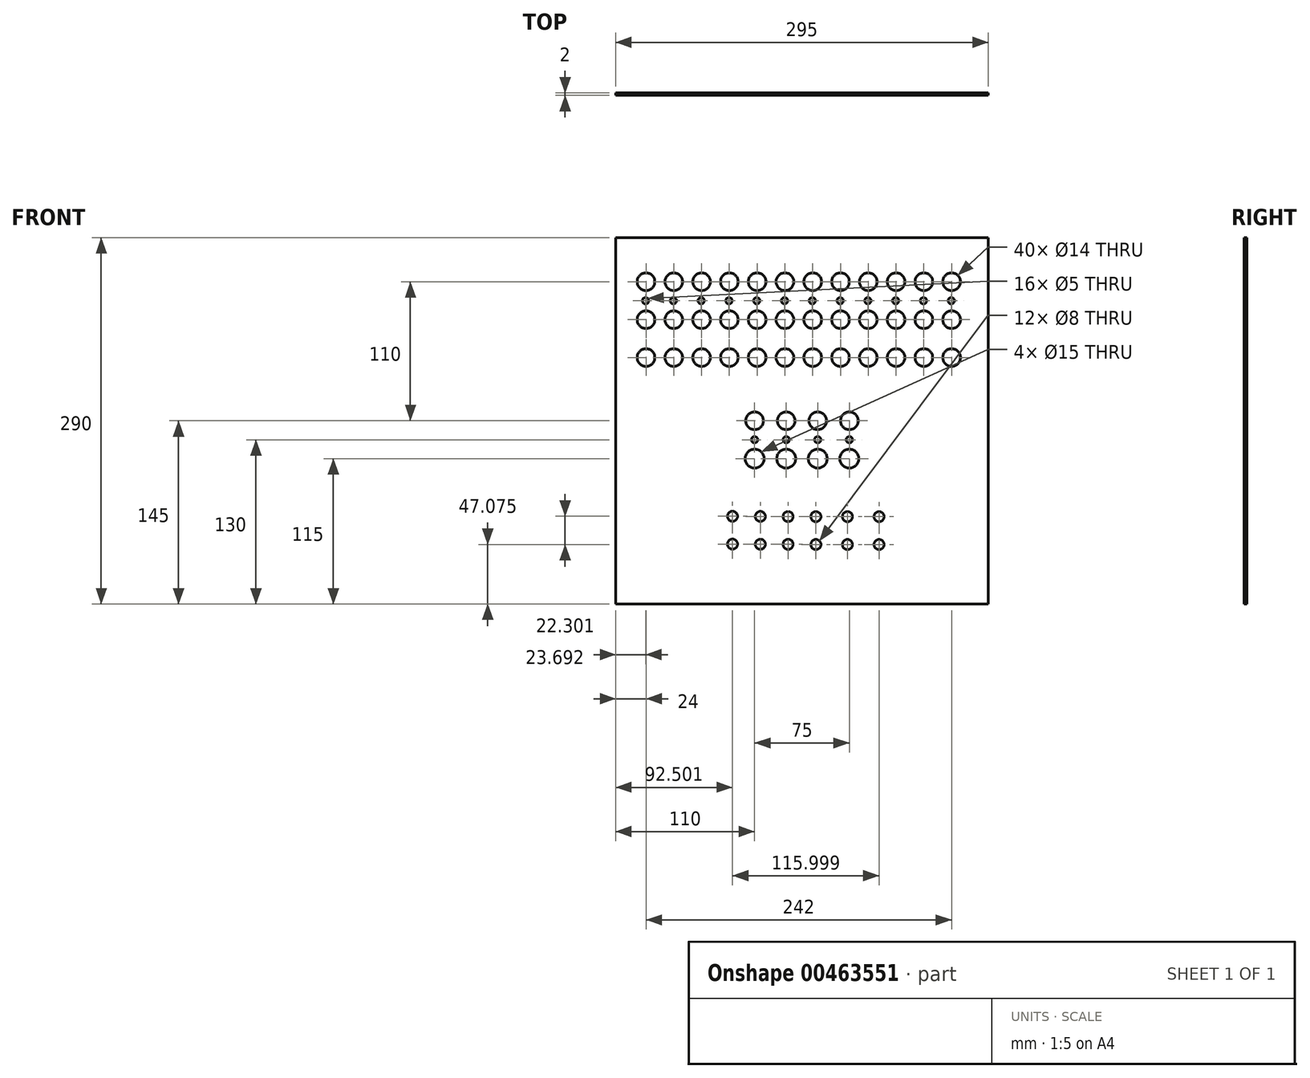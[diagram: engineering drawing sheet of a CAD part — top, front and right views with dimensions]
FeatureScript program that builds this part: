
annotation { "Feature Type Name" : "Feature", "Feature Type Description" : "" }
export const myFeature = defineFeature(function(context is Context, id is Id, definition is map)
    precondition{}
    {
        {
            var Q0;
            Q0=qCreatedBy(makeId("Front.planeOp"),FACE);
            var sketch = newSketch(context, id + "F0", { "sketchPlane" : qUnion([Q0])});
            skLineSegment(sketch, "E0.bottom", {"start": v(147.5, 145) * mm, "end": v(-147.5, 145) * mm});
            skLineSegment(sketch, "E0.top", {"start": v(147.5, -145) * mm, "end": v(-147.5, -145) * mm});
            skLineSegment(sketch, "E0.left", {"start": v(147.5, 145) * mm, "end": v(147.5, -145) * mm});
            skLineSegment(sketch, "E0.right", {"start": v(-147.5, 145) * mm, "end": v(-147.5, -145) * mm});
            skPoint(sketch, "E0.middle", {"position": v(0, 0) * mm});
            skSolve(sketch);
        }
        {
            var Q0;
            Q0=makeQuery(id+"F0.imprint","IMPRINT",FACE,{"disambiguationData":[TD([[makeQuery(id+"F0.imprint","IMPRINT",EDGE,{"derivedFrom":sQuery(id+"F0.wireOp",EDGE,"E0.bottom")}),1.0]])]});
            extrude(context, id + "F1", {"entities" : qUnion([Q0]), "oppositeDirection" : true, "depth" : 2 * mm, "offsetDistance" : 25 * mm});
        }
        {
            var Q0;
            Q0=makeQuery(id+"F1.opExtrude","CAP_FACE",FACE,{"disambiguationData":[OSD([sQuery(id+"F0.wireOp",EDGE,"E0.bottom"),sQuery(id+"F0.wireOp",EDGE,"E0.top"),sQuery(id+"F0.wireOp",EDGE,"E0.left"),sQuery(id+"F0.wireOp",EDGE,"E0.right")])],"isStart":true});
            var sketch = newSketch(context, id + "F2", { "sketchPlane" : qUnion([Q0])});
            skLineSegment(sketch, "E1", {"start": v(-147.5, 110) * mm, "end": v(322.56, 110) * mm});
            skCircle(sketch, "E2", {"center": v(-123.5, 110) * mm, "radius": 7 * mm});
            skLineSegment(sketch, "E3.direction1", {"start": v(-120.5, 110) * mm, "end": v(-98.5, 110) * mm, "construction": true});
            skCircle(sketch, "E4.1.0.0", {"center": v(-101.5, 110) * mm, "radius": 7 * mm});
            skCircle(sketch, "E4.2.0.0", {"center": v(-79.5, 110) * mm, "radius": 7 * mm});
            skCircle(sketch, "E4.3.0.0", {"center": v(-57.5, 110) * mm, "radius": 7 * mm});
            skCircle(sketch, "E4.4.0.0", {"center": v(-35.5, 110) * mm, "radius": 7 * mm});
            skCircle(sketch, "E4.5.0.0", {"center": v(-13.5, 110) * mm, "radius": 7 * mm});
            skCircle(sketch, "E4.6.0.0", {"center": v(8.5, 110) * mm, "radius": 7 * mm});
            skCircle(sketch, "E4.7.0.0", {"center": v(30.5, 110) * mm, "radius": 7 * mm});
            skCircle(sketch, "E4.8.0.0", {"center": v(52.5, 110) * mm, "radius": 7 * mm});
            skCircle(sketch, "E4.9.0.0", {"center": v(74.5, 110) * mm, "radius": 7 * mm});
            skCircle(sketch, "E4.10.0.0", {"center": v(96.5, 110) * mm, "radius": 7 * mm});
            skCircle(sketch, "E4.11.0.0", {"center": v(118.5, 110) * mm, "radius": 7 * mm});
            skLineSegment(sketch, "E4.direction1", {"start": v(-123.5, 110) * mm, "end": v(-101.5, 110) * mm, "construction": true});
            skSolve(sketch);
        }
        {
            var Q0;
            {var subQ0=sQuery(id+"F2.wireOp",EDGE,"E2");var subQ1=sQuery(id+"F2.wireOp",EDGE,"E1");var subQ2=makeQuery(id+"F2.imprint","INTERSECT",VERTEX,{"disambiguationData":[OD(0.0)],"derivedFrom":[subQ1,subQ0]});Q0=makeQuery(id+"F2.imprint","IMPRINT",FACE,{"disambiguationData":[TD([[makeQuery(id+"F2.imprint","IMPRINT",EDGE,{"disambiguationData":[TD([[subQ2,-1.0]])],"derivedFrom":subQ1}),1.0]])]});}
            var Q1;
            {var subQ0=sQuery(id+"F2.wireOp",EDGE,"E2");var subQ1=sQuery(id+"F2.wireOp",EDGE,"E1");var subQ2=makeQuery(id+"F2.imprint","INTERSECT",VERTEX,{"disambiguationData":[OD(0.0)],"derivedFrom":[subQ1,subQ0]});Q1=makeQuery(id+"F2.imprint","IMPRINT",FACE,{"disambiguationData":[TD([[makeQuery(id+"F2.imprint","IMPRINT",EDGE,{"disambiguationData":[TD([[subQ2,-1.0]])],"derivedFrom":subQ1}),-1.0]])]});}
            var Q2;
            Q2=sQuery(id+"F2.wireOp",EDGE,"E2");
            extrude(context, id + "F3", {"entities" : qUnion([Q0, Q1]), "operationType" : NewBodyOperationType.REMOVE, "surfaceEntities" : qUnion([Q2]), "oppositeDirection" : true, "depth" : 25 * mm, "offsetDistance" : 25 * mm});
        }
        {
            var Q0;
            Q0 = qSketchRegion(id + "F2", true);
            extrude(context, id + "F4", {"entities" : qUnion([Q0]), "operationType" : NewBodyOperationType.REMOVE, "oppositeDirection" : true, "depth" : 25 * mm, "offsetDistance" : 25 * mm});
        }
        {
            var Q0;
            Q0=makeQuery(id+"F1.opExtrude","CAP_FACE",FACE,{"disambiguationData":[OSD([sQuery(id+"F0.wireOp",EDGE,"E0.bottom"),sQuery(id+"F0.wireOp",EDGE,"E0.top"),sQuery(id+"F0.wireOp",EDGE,"E0.left"),sQuery(id+"F0.wireOp",EDGE,"E0.right")])],"isStart":true});
            var sketch = newSketch(context, id + "F5", { "sketchPlane" : qUnion([Q0])});
            skLineSegment(sketch, "E5", {"start": v(-147.5, 80) * mm, "end": v(147.5, 80) * mm});
            skLineSegment(sketch, "E6", {"start": v(147.5, 50) * mm, "end": v(-147.5, 50) * mm});
            skLineSegment(sketch, "E7", {"start": v(-147.5, 110) * mm, "end": v(147.5, 110) * mm});
            skCircle(sketch, "E8", {"center": v(-123.5, 80) * mm, "radius": 7 * mm});
            skCircle(sketch, "E9", {"center": v(-123.5, 50) * mm, "radius": 7 * mm});
            skCircle(sketch, "E10.1.0.0", {"center": v(-101.5, 80) * mm, "radius": 7 * mm});
            skCircle(sketch, "E10.1.0.1", {"center": v(-101.5, 50) * mm, "radius": 7 * mm});
            skCircle(sketch, "E10.2.0.0", {"center": v(-79.5, 80) * mm, "radius": 7 * mm});
            skCircle(sketch, "E10.2.0.1", {"center": v(-79.5, 50) * mm, "radius": 7 * mm});
            skCircle(sketch, "E10.3.0.0", {"center": v(-57.5, 80) * mm, "radius": 7 * mm});
            skCircle(sketch, "E10.3.0.1", {"center": v(-57.5, 50) * mm, "radius": 7 * mm});
            skCircle(sketch, "E10.4.0.0", {"center": v(-35.5, 80) * mm, "radius": 7 * mm});
            skCircle(sketch, "E10.4.0.1", {"center": v(-35.5, 50) * mm, "radius": 7 * mm});
            skCircle(sketch, "E10.5.0.0", {"center": v(-13.5, 80) * mm, "radius": 7 * mm});
            skCircle(sketch, "E10.5.0.1", {"center": v(-13.5, 50) * mm, "radius": 7 * mm});
            skCircle(sketch, "E10.6.0.0", {"center": v(8.5, 80) * mm, "radius": 7 * mm});
            skCircle(sketch, "E10.6.0.1", {"center": v(8.5, 50) * mm, "radius": 7 * mm});
            skCircle(sketch, "E10.7.0.0", {"center": v(30.5, 80) * mm, "radius": 7 * mm});
            skCircle(sketch, "E10.7.0.1", {"center": v(30.5, 50) * mm, "radius": 7 * mm});
            skCircle(sketch, "E10.8.0.0", {"center": v(52.5, 80) * mm, "radius": 7 * mm});
            skCircle(sketch, "E10.8.0.1", {"center": v(52.5, 50) * mm, "radius": 7 * mm});
            skCircle(sketch, "E10.9.0.0", {"center": v(74.5, 80) * mm, "radius": 7 * mm});
            skCircle(sketch, "E10.9.0.1", {"center": v(74.5, 50) * mm, "radius": 7 * mm});
            skCircle(sketch, "E10.10.0.0", {"center": v(96.5, 80) * mm, "radius": 7 * mm});
            skCircle(sketch, "E10.10.0.1", {"center": v(96.5, 50) * mm, "radius": 7 * mm});
            skCircle(sketch, "E10.11.0.0", {"center": v(118.5, 80) * mm, "radius": 7 * mm});
            skCircle(sketch, "E10.11.0.1", {"center": v(118.5, 50) * mm, "radius": 7 * mm});
            skLineSegment(sketch, "E10.direction1", {"start": v(-123.5, 80) * mm, "end": v(-101.5, 80) * mm, "construction": true});
            skSolve(sketch);
        }
        {
            var Q0;
            {var subQ0=sQuery(id+"F5.wireOp",EDGE,"E8");var subQ1=sQuery(id+"F5.wireOp",EDGE,"E5");var subQ2=makeQuery(id+"F5.imprint","INTERSECT",VERTEX,{"disambiguationData":[OD(0.0)],"derivedFrom":[subQ1,subQ0]});Q0=makeQuery(id+"F5.imprint","IMPRINT",FACE,{"disambiguationData":[TD([[makeQuery(id+"F5.imprint","IMPRINT",EDGE,{"disambiguationData":[TD([[subQ2,-1.0]])],"derivedFrom":subQ1}),1.0]])]});}
            var Q1;
            {var subQ0=sQuery(id+"F5.wireOp",EDGE,"E8");var subQ1=sQuery(id+"F5.wireOp",EDGE,"E5");var subQ2=makeQuery(id+"F5.imprint","INTERSECT",VERTEX,{"disambiguationData":[OD(0.0)],"derivedFrom":[subQ1,subQ0]});Q1=makeQuery(id+"F5.imprint","IMPRINT",FACE,{"disambiguationData":[TD([[makeQuery(id+"F5.imprint","IMPRINT",EDGE,{"disambiguationData":[TD([[subQ2,-1.0]])],"derivedFrom":subQ1}),-1.0]])]});}
            var Q2;
            {var subQ0=sQuery(id+"F5.wireOp",EDGE,"E9");var subQ1=sQuery(id+"F5.wireOp",EDGE,"E6");var subQ2=makeQuery(id+"F5.imprint","INTERSECT",VERTEX,{"disambiguationData":[OD(0.0)],"derivedFrom":[subQ1,subQ0]});Q2=makeQuery(id+"F5.imprint","IMPRINT",FACE,{"disambiguationData":[TD([[makeQuery(id+"F5.imprint","IMPRINT",EDGE,{"disambiguationData":[TD([[subQ2,-1.0]])],"derivedFrom":subQ1}),-1.0]])]});}
            var Q3;
            {var subQ0=sQuery(id+"F5.wireOp",EDGE,"E9");var subQ1=sQuery(id+"F5.wireOp",EDGE,"E6");var subQ2=makeQuery(id+"F5.imprint","INTERSECT",VERTEX,{"disambiguationData":[OD(0.0)],"derivedFrom":[subQ1,subQ0]});Q3=makeQuery(id+"F5.imprint","IMPRINT",FACE,{"disambiguationData":[TD([[makeQuery(id+"F5.imprint","IMPRINT",EDGE,{"disambiguationData":[TD([[subQ2,-1.0]])],"derivedFrom":subQ1}),1.0]])]});}
            var Q4;
            {var subQ0=sQuery(id+"F5.wireOp",EDGE,"E10.1.0.0");var subQ1=sQuery(id+"F5.wireOp",EDGE,"E5");var subQ2=makeQuery(id+"F5.imprint","INTERSECT",VERTEX,{"disambiguationData":[OD(0.0)],"derivedFrom":[subQ1,subQ0]});Q4=makeQuery(id+"F5.imprint","IMPRINT",FACE,{"disambiguationData":[TD([[makeQuery(id+"F5.imprint","IMPRINT",EDGE,{"disambiguationData":[TD([[subQ2,-1.0]])],"derivedFrom":subQ1}),1.0]])]});}
            var Q5;
            {var subQ0=sQuery(id+"F5.wireOp",EDGE,"E10.1.0.0");var subQ1=sQuery(id+"F5.wireOp",EDGE,"E5");var subQ2=makeQuery(id+"F5.imprint","INTERSECT",VERTEX,{"disambiguationData":[OD(0.0)],"derivedFrom":[subQ1,subQ0]});Q5=makeQuery(id+"F5.imprint","IMPRINT",FACE,{"disambiguationData":[TD([[makeQuery(id+"F5.imprint","IMPRINT",EDGE,{"disambiguationData":[TD([[subQ2,-1.0]])],"derivedFrom":subQ1}),-1.0]])]});}
            var Q6;
            {var subQ0=sQuery(id+"F5.wireOp",EDGE,"E10.2.0.0");var subQ1=sQuery(id+"F5.wireOp",EDGE,"E5");var subQ2=makeQuery(id+"F5.imprint","INTERSECT",VERTEX,{"disambiguationData":[OD(0.0)],"derivedFrom":[subQ1,subQ0]});Q6=makeQuery(id+"F5.imprint","IMPRINT",FACE,{"disambiguationData":[TD([[makeQuery(id+"F5.imprint","IMPRINT",EDGE,{"disambiguationData":[TD([[subQ2,-1.0]])],"derivedFrom":subQ1}),1.0]])]});}
            var Q7;
            {var subQ0=sQuery(id+"F5.wireOp",EDGE,"E10.2.0.0");var subQ1=sQuery(id+"F5.wireOp",EDGE,"E5");var subQ2=makeQuery(id+"F5.imprint","INTERSECT",VERTEX,{"disambiguationData":[OD(0.0)],"derivedFrom":[subQ1,subQ0]});Q7=makeQuery(id+"F5.imprint","IMPRINT",FACE,{"disambiguationData":[TD([[makeQuery(id+"F5.imprint","IMPRINT",EDGE,{"disambiguationData":[TD([[subQ2,-1.0]])],"derivedFrom":subQ1}),-1.0]])]});}
            var Q8;
            {var subQ0=sQuery(id+"F5.wireOp",EDGE,"E10.3.0.0");var subQ1=sQuery(id+"F5.wireOp",EDGE,"E5");var subQ2=makeQuery(id+"F5.imprint","INTERSECT",VERTEX,{"disambiguationData":[OD(0.0)],"derivedFrom":[subQ1,subQ0]});Q8=makeQuery(id+"F5.imprint","IMPRINT",FACE,{"disambiguationData":[TD([[makeQuery(id+"F5.imprint","IMPRINT",EDGE,{"disambiguationData":[TD([[subQ2,-1.0]])],"derivedFrom":subQ1}),1.0]])]});}
            var Q9;
            {var subQ0=sQuery(id+"F5.wireOp",EDGE,"E10.3.0.0");var subQ1=sQuery(id+"F5.wireOp",EDGE,"E5");var subQ2=makeQuery(id+"F5.imprint","INTERSECT",VERTEX,{"disambiguationData":[OD(0.0)],"derivedFrom":[subQ1,subQ0]});Q9=makeQuery(id+"F5.imprint","IMPRINT",FACE,{"disambiguationData":[TD([[makeQuery(id+"F5.imprint","IMPRINT",EDGE,{"disambiguationData":[TD([[subQ2,-1.0]])],"derivedFrom":subQ1}),-1.0]])]});}
            var Q10;
            {var subQ0=sQuery(id+"F5.wireOp",EDGE,"E10.4.0.0");var subQ1=sQuery(id+"F5.wireOp",EDGE,"E5");var subQ2=makeQuery(id+"F5.imprint","INTERSECT",VERTEX,{"disambiguationData":[OD(0.0)],"derivedFrom":[subQ1,subQ0]});Q10=makeQuery(id+"F5.imprint","IMPRINT",FACE,{"disambiguationData":[TD([[makeQuery(id+"F5.imprint","IMPRINT",EDGE,{"disambiguationData":[TD([[subQ2,-1.0]])],"derivedFrom":subQ1}),1.0]])]});}
            var Q11;
            {var subQ0=sQuery(id+"F5.wireOp",EDGE,"E10.4.0.0");var subQ1=sQuery(id+"F5.wireOp",EDGE,"E5");var subQ2=makeQuery(id+"F5.imprint","INTERSECT",VERTEX,{"disambiguationData":[OD(0.0)],"derivedFrom":[subQ1,subQ0]});Q11=makeQuery(id+"F5.imprint","IMPRINT",FACE,{"disambiguationData":[TD([[makeQuery(id+"F5.imprint","IMPRINT",EDGE,{"disambiguationData":[TD([[subQ2,-1.0]])],"derivedFrom":subQ1}),-1.0]])]});}
            var Q12;
            {var subQ0=sQuery(id+"F5.wireOp",EDGE,"E10.5.0.0");var subQ1=sQuery(id+"F5.wireOp",EDGE,"E5");var subQ2=makeQuery(id+"F5.imprint","INTERSECT",VERTEX,{"disambiguationData":[OD(0.0)],"derivedFrom":[subQ1,subQ0]});Q12=makeQuery(id+"F5.imprint","IMPRINT",FACE,{"disambiguationData":[TD([[makeQuery(id+"F5.imprint","IMPRINT",EDGE,{"disambiguationData":[TD([[subQ2,-1.0]])],"derivedFrom":subQ1}),1.0]])]});}
            var Q13;
            {var subQ0=sQuery(id+"F5.wireOp",EDGE,"E10.5.0.0");var subQ1=sQuery(id+"F5.wireOp",EDGE,"E5");var subQ2=makeQuery(id+"F5.imprint","INTERSECT",VERTEX,{"disambiguationData":[OD(0.0)],"derivedFrom":[subQ1,subQ0]});Q13=makeQuery(id+"F5.imprint","IMPRINT",FACE,{"disambiguationData":[TD([[makeQuery(id+"F5.imprint","IMPRINT",EDGE,{"disambiguationData":[TD([[subQ2,-1.0]])],"derivedFrom":subQ1}),-1.0]])]});}
            var Q14;
            {var subQ0=sQuery(id+"F5.wireOp",EDGE,"E10.6.0.0");var subQ1=sQuery(id+"F5.wireOp",EDGE,"E5");var subQ2=makeQuery(id+"F5.imprint","INTERSECT",VERTEX,{"disambiguationData":[OD(0.0)],"derivedFrom":[subQ1,subQ0]});Q14=makeQuery(id+"F5.imprint","IMPRINT",FACE,{"disambiguationData":[TD([[makeQuery(id+"F5.imprint","IMPRINT",EDGE,{"disambiguationData":[TD([[subQ2,-1.0]])],"derivedFrom":subQ1}),1.0]])]});}
            var Q15;
            {var subQ0=sQuery(id+"F5.wireOp",EDGE,"E10.6.0.0");var subQ1=sQuery(id+"F5.wireOp",EDGE,"E5");var subQ2=makeQuery(id+"F5.imprint","INTERSECT",VERTEX,{"disambiguationData":[OD(0.0)],"derivedFrom":[subQ1,subQ0]});Q15=makeQuery(id+"F5.imprint","IMPRINT",FACE,{"disambiguationData":[TD([[makeQuery(id+"F5.imprint","IMPRINT",EDGE,{"disambiguationData":[TD([[subQ2,-1.0]])],"derivedFrom":subQ1}),-1.0]])]});}
            var Q16;
            {var subQ0=sQuery(id+"F5.wireOp",EDGE,"E10.7.0.0");var subQ1=sQuery(id+"F5.wireOp",EDGE,"E5");var subQ2=makeQuery(id+"F5.imprint","INTERSECT",VERTEX,{"disambiguationData":[OD(0.0)],"derivedFrom":[subQ1,subQ0]});Q16=makeQuery(id+"F5.imprint","IMPRINT",FACE,{"disambiguationData":[TD([[makeQuery(id+"F5.imprint","IMPRINT",EDGE,{"disambiguationData":[TD([[subQ2,-1.0]])],"derivedFrom":subQ1}),1.0]])]});}
            var Q17;
            {var subQ0=sQuery(id+"F5.wireOp",EDGE,"E10.7.0.0");var subQ1=sQuery(id+"F5.wireOp",EDGE,"E5");var subQ2=makeQuery(id+"F5.imprint","INTERSECT",VERTEX,{"disambiguationData":[OD(0.0)],"derivedFrom":[subQ1,subQ0]});Q17=makeQuery(id+"F5.imprint","IMPRINT",FACE,{"disambiguationData":[TD([[makeQuery(id+"F5.imprint","IMPRINT",EDGE,{"disambiguationData":[TD([[subQ2,-1.0]])],"derivedFrom":subQ1}),-1.0]])]});}
            var Q18;
            {var subQ0=sQuery(id+"F5.wireOp",EDGE,"E10.8.0.0");var subQ1=sQuery(id+"F5.wireOp",EDGE,"E5");var subQ2=makeQuery(id+"F5.imprint","INTERSECT",VERTEX,{"disambiguationData":[OD(0.0)],"derivedFrom":[subQ1,subQ0]});Q18=makeQuery(id+"F5.imprint","IMPRINT",FACE,{"disambiguationData":[TD([[makeQuery(id+"F5.imprint","IMPRINT",EDGE,{"disambiguationData":[TD([[subQ2,-1.0]])],"derivedFrom":subQ1}),-1.0]])]});}
            var Q19;
            {var subQ0=sQuery(id+"F5.wireOp",EDGE,"E10.9.0.0");var subQ1=sQuery(id+"F5.wireOp",EDGE,"E5");var subQ2=makeQuery(id+"F5.imprint","INTERSECT",VERTEX,{"disambiguationData":[OD(0.0)],"derivedFrom":[subQ1,subQ0]});Q19=makeQuery(id+"F5.imprint","IMPRINT",FACE,{"disambiguationData":[TD([[makeQuery(id+"F5.imprint","IMPRINT",EDGE,{"disambiguationData":[TD([[subQ2,-1.0]])],"derivedFrom":subQ1}),-1.0]])]});}
            var Q20;
            {var subQ0=sQuery(id+"F5.wireOp",EDGE,"E10.10.0.0");var subQ1=sQuery(id+"F5.wireOp",EDGE,"E5");var subQ2=makeQuery(id+"F5.imprint","INTERSECT",VERTEX,{"disambiguationData":[OD(0.0)],"derivedFrom":[subQ1,subQ0]});Q20=makeQuery(id+"F5.imprint","IMPRINT",FACE,{"disambiguationData":[TD([[makeQuery(id+"F5.imprint","IMPRINT",EDGE,{"disambiguationData":[TD([[subQ2,-1.0]])],"derivedFrom":subQ1}),-1.0]])]});}
            var Q21;
            {var subQ0=sQuery(id+"F5.wireOp",EDGE,"E10.11.0.0");var subQ1=sQuery(id+"F5.wireOp",EDGE,"E5");var subQ2=makeQuery(id+"F5.imprint","INTERSECT",VERTEX,{"disambiguationData":[OD(0.0)],"derivedFrom":[subQ1,subQ0]});Q21=makeQuery(id+"F5.imprint","IMPRINT",FACE,{"disambiguationData":[TD([[makeQuery(id+"F5.imprint","IMPRINT",EDGE,{"disambiguationData":[TD([[subQ2,-1.0]])],"derivedFrom":subQ1}),-1.0]])]});}
            var Q22;
            {var subQ0=sQuery(id+"F5.wireOp",EDGE,"E10.11.0.0");var subQ1=sQuery(id+"F5.wireOp",EDGE,"E5");var subQ2=makeQuery(id+"F5.imprint","INTERSECT",VERTEX,{"disambiguationData":[OD(0.0)],"derivedFrom":[subQ1,subQ0]});Q22=makeQuery(id+"F5.imprint","IMPRINT",FACE,{"disambiguationData":[TD([[makeQuery(id+"F5.imprint","IMPRINT",EDGE,{"disambiguationData":[TD([[subQ2,-1.0]])],"derivedFrom":subQ1}),1.0]])]});}
            var Q23;
            {var subQ0=sQuery(id+"F5.wireOp",EDGE,"E10.10.0.0");var subQ1=sQuery(id+"F5.wireOp",EDGE,"E5");var subQ2=makeQuery(id+"F5.imprint","INTERSECT",VERTEX,{"disambiguationData":[OD(0.0)],"derivedFrom":[subQ1,subQ0]});Q23=makeQuery(id+"F5.imprint","IMPRINT",FACE,{"disambiguationData":[TD([[makeQuery(id+"F5.imprint","IMPRINT",EDGE,{"disambiguationData":[TD([[subQ2,-1.0]])],"derivedFrom":subQ1}),1.0]])]});}
            var Q24;
            {var subQ0=sQuery(id+"F5.wireOp",EDGE,"E10.9.0.0");var subQ1=sQuery(id+"F5.wireOp",EDGE,"E5");var subQ2=makeQuery(id+"F5.imprint","INTERSECT",VERTEX,{"disambiguationData":[OD(0.0)],"derivedFrom":[subQ1,subQ0]});Q24=makeQuery(id+"F5.imprint","IMPRINT",FACE,{"disambiguationData":[TD([[makeQuery(id+"F5.imprint","IMPRINT",EDGE,{"disambiguationData":[TD([[subQ2,-1.0]])],"derivedFrom":subQ1}),1.0]])]});}
            var Q25;
            {var subQ0=sQuery(id+"F5.wireOp",EDGE,"E10.8.0.0");var subQ1=sQuery(id+"F5.wireOp",EDGE,"E5");var subQ2=makeQuery(id+"F5.imprint","INTERSECT",VERTEX,{"disambiguationData":[OD(0.0)],"derivedFrom":[subQ1,subQ0]});Q25=makeQuery(id+"F5.imprint","IMPRINT",FACE,{"disambiguationData":[TD([[makeQuery(id+"F5.imprint","IMPRINT",EDGE,{"disambiguationData":[TD([[subQ2,-1.0]])],"derivedFrom":subQ1}),1.0]])]});}
            var Q26;
            {var subQ0=sQuery(id+"F5.wireOp",EDGE,"E10.11.0.1");var subQ1=sQuery(id+"F5.wireOp",EDGE,"E6");var subQ2=makeQuery(id+"F5.imprint","INTERSECT",VERTEX,{"disambiguationData":[OD(0.0)],"derivedFrom":[subQ1,subQ0]});Q26=makeQuery(id+"F5.imprint","IMPRINT",FACE,{"disambiguationData":[TD([[makeQuery(id+"F5.imprint","IMPRINT",EDGE,{"disambiguationData":[TD([[subQ2,-1.0]])],"derivedFrom":subQ1}),-1.0]])]});}
            var Q27;
            {var subQ0=sQuery(id+"F5.wireOp",EDGE,"E10.10.0.1");var subQ1=sQuery(id+"F5.wireOp",EDGE,"E6");var subQ2=makeQuery(id+"F5.imprint","INTERSECT",VERTEX,{"disambiguationData":[OD(0.0)],"derivedFrom":[subQ1,subQ0]});Q27=makeQuery(id+"F5.imprint","IMPRINT",FACE,{"disambiguationData":[TD([[makeQuery(id+"F5.imprint","IMPRINT",EDGE,{"disambiguationData":[TD([[subQ2,-1.0]])],"derivedFrom":subQ1}),-1.0]])]});}
            var Q28;
            {var subQ0=sQuery(id+"F5.wireOp",EDGE,"E10.10.0.1");var subQ1=sQuery(id+"F5.wireOp",EDGE,"E6");var subQ2=makeQuery(id+"F5.imprint","INTERSECT",VERTEX,{"disambiguationData":[OD(0.0)],"derivedFrom":[subQ1,subQ0]});Q28=makeQuery(id+"F5.imprint","IMPRINT",FACE,{"disambiguationData":[TD([[makeQuery(id+"F5.imprint","IMPRINT",EDGE,{"disambiguationData":[TD([[subQ2,-1.0]])],"derivedFrom":subQ1}),1.0]])]});}
            var Q29;
            {var subQ0=sQuery(id+"F5.wireOp",EDGE,"E10.11.0.1");var subQ1=sQuery(id+"F5.wireOp",EDGE,"E6");var subQ2=makeQuery(id+"F5.imprint","INTERSECT",VERTEX,{"disambiguationData":[OD(0.0)],"derivedFrom":[subQ1,subQ0]});Q29=makeQuery(id+"F5.imprint","IMPRINT",FACE,{"disambiguationData":[TD([[makeQuery(id+"F5.imprint","IMPRINT",EDGE,{"disambiguationData":[TD([[subQ2,-1.0]])],"derivedFrom":subQ1}),1.0]])]});}
            var Q30;
            {var subQ0=sQuery(id+"F5.wireOp",EDGE,"E10.9.0.1");var subQ1=sQuery(id+"F5.wireOp",EDGE,"E6");var subQ2=makeQuery(id+"F5.imprint","INTERSECT",VERTEX,{"disambiguationData":[OD(0.0)],"derivedFrom":[subQ1,subQ0]});Q30=makeQuery(id+"F5.imprint","IMPRINT",FACE,{"disambiguationData":[TD([[makeQuery(id+"F5.imprint","IMPRINT",EDGE,{"disambiguationData":[TD([[subQ2,-1.0]])],"derivedFrom":subQ1}),-1.0]])]});}
            var Q31;
            {var subQ0=sQuery(id+"F5.wireOp",EDGE,"E10.9.0.1");var subQ1=sQuery(id+"F5.wireOp",EDGE,"E6");var subQ2=makeQuery(id+"F5.imprint","INTERSECT",VERTEX,{"disambiguationData":[OD(0.0)],"derivedFrom":[subQ1,subQ0]});Q31=makeQuery(id+"F5.imprint","IMPRINT",FACE,{"disambiguationData":[TD([[makeQuery(id+"F5.imprint","IMPRINT",EDGE,{"disambiguationData":[TD([[subQ2,-1.0]])],"derivedFrom":subQ1}),1.0]])]});}
            var Q32;
            {var subQ0=sQuery(id+"F5.wireOp",EDGE,"E10.8.0.1");var subQ1=sQuery(id+"F5.wireOp",EDGE,"E6");var subQ2=makeQuery(id+"F5.imprint","INTERSECT",VERTEX,{"disambiguationData":[OD(0.0)],"derivedFrom":[subQ1,subQ0]});Q32=makeQuery(id+"F5.imprint","IMPRINT",FACE,{"disambiguationData":[TD([[makeQuery(id+"F5.imprint","IMPRINT",EDGE,{"disambiguationData":[TD([[subQ2,-1.0]])],"derivedFrom":subQ1}),1.0]])]});}
            var Q33;
            {var subQ0=sQuery(id+"F5.wireOp",EDGE,"E10.8.0.1");var subQ1=sQuery(id+"F5.wireOp",EDGE,"E6");var subQ2=makeQuery(id+"F5.imprint","INTERSECT",VERTEX,{"disambiguationData":[OD(0.0)],"derivedFrom":[subQ1,subQ0]});Q33=makeQuery(id+"F5.imprint","IMPRINT",FACE,{"disambiguationData":[TD([[makeQuery(id+"F5.imprint","IMPRINT",EDGE,{"disambiguationData":[TD([[subQ2,-1.0]])],"derivedFrom":subQ1}),-1.0]])]});}
            var Q34;
            {var subQ0=sQuery(id+"F5.wireOp",EDGE,"E10.7.0.1");var subQ1=sQuery(id+"F5.wireOp",EDGE,"E6");var subQ2=makeQuery(id+"F5.imprint","INTERSECT",VERTEX,{"disambiguationData":[OD(0.0)],"derivedFrom":[subQ1,subQ0]});Q34=makeQuery(id+"F5.imprint","IMPRINT",FACE,{"disambiguationData":[TD([[makeQuery(id+"F5.imprint","IMPRINT",EDGE,{"disambiguationData":[TD([[subQ2,-1.0]])],"derivedFrom":subQ1}),-1.0]])]});}
            var Q35;
            {var subQ0=sQuery(id+"F5.wireOp",EDGE,"E10.7.0.1");var subQ1=sQuery(id+"F5.wireOp",EDGE,"E6");var subQ2=makeQuery(id+"F5.imprint","INTERSECT",VERTEX,{"disambiguationData":[OD(0.0)],"derivedFrom":[subQ1,subQ0]});Q35=makeQuery(id+"F5.imprint","IMPRINT",FACE,{"disambiguationData":[TD([[makeQuery(id+"F5.imprint","IMPRINT",EDGE,{"disambiguationData":[TD([[subQ2,-1.0]])],"derivedFrom":subQ1}),1.0]])]});}
            var Q36;
            {var subQ0=sQuery(id+"F5.wireOp",EDGE,"E10.6.0.1");var subQ1=sQuery(id+"F5.wireOp",EDGE,"E6");var subQ2=makeQuery(id+"F5.imprint","INTERSECT",VERTEX,{"disambiguationData":[OD(0.0)],"derivedFrom":[subQ1,subQ0]});Q36=makeQuery(id+"F5.imprint","IMPRINT",FACE,{"disambiguationData":[TD([[makeQuery(id+"F5.imprint","IMPRINT",EDGE,{"disambiguationData":[TD([[subQ2,-1.0]])],"derivedFrom":subQ1}),-1.0]])]});}
            var Q37;
            {var subQ0=sQuery(id+"F5.wireOp",EDGE,"E10.6.0.1");var subQ1=sQuery(id+"F5.wireOp",EDGE,"E6");var subQ2=makeQuery(id+"F5.imprint","INTERSECT",VERTEX,{"disambiguationData":[OD(0.0)],"derivedFrom":[subQ1,subQ0]});Q37=makeQuery(id+"F5.imprint","IMPRINT",FACE,{"disambiguationData":[TD([[makeQuery(id+"F5.imprint","IMPRINT",EDGE,{"disambiguationData":[TD([[subQ2,-1.0]])],"derivedFrom":subQ1}),1.0]])]});}
            var Q38;
            {var subQ0=sQuery(id+"F5.wireOp",EDGE,"E10.5.0.1");var subQ1=sQuery(id+"F5.wireOp",EDGE,"E6");var subQ2=makeQuery(id+"F5.imprint","INTERSECT",VERTEX,{"disambiguationData":[OD(0.0)],"derivedFrom":[subQ1,subQ0]});Q38=makeQuery(id+"F5.imprint","IMPRINT",FACE,{"disambiguationData":[TD([[makeQuery(id+"F5.imprint","IMPRINT",EDGE,{"disambiguationData":[TD([[subQ2,-1.0]])],"derivedFrom":subQ1}),-1.0]])]});}
            var Q39;
            {var subQ0=sQuery(id+"F5.wireOp",EDGE,"E10.5.0.1");var subQ1=sQuery(id+"F5.wireOp",EDGE,"E6");var subQ2=makeQuery(id+"F5.imprint","INTERSECT",VERTEX,{"disambiguationData":[OD(0.0)],"derivedFrom":[subQ1,subQ0]});Q39=makeQuery(id+"F5.imprint","IMPRINT",FACE,{"disambiguationData":[TD([[makeQuery(id+"F5.imprint","IMPRINT",EDGE,{"disambiguationData":[TD([[subQ2,-1.0]])],"derivedFrom":subQ1}),1.0]])]});}
            var Q40;
            {var subQ0=sQuery(id+"F5.wireOp",EDGE,"E10.4.0.1");var subQ1=sQuery(id+"F5.wireOp",EDGE,"E6");var subQ2=makeQuery(id+"F5.imprint","INTERSECT",VERTEX,{"disambiguationData":[OD(0.0)],"derivedFrom":[subQ1,subQ0]});Q40=makeQuery(id+"F5.imprint","IMPRINT",FACE,{"disambiguationData":[TD([[makeQuery(id+"F5.imprint","IMPRINT",EDGE,{"disambiguationData":[TD([[subQ2,-1.0]])],"derivedFrom":subQ1}),-1.0]])]});}
            var Q41;
            {var subQ0=sQuery(id+"F5.wireOp",EDGE,"E10.4.0.1");var subQ1=sQuery(id+"F5.wireOp",EDGE,"E6");var subQ2=makeQuery(id+"F5.imprint","INTERSECT",VERTEX,{"disambiguationData":[OD(0.0)],"derivedFrom":[subQ1,subQ0]});Q41=makeQuery(id+"F5.imprint","IMPRINT",FACE,{"disambiguationData":[TD([[makeQuery(id+"F5.imprint","IMPRINT",EDGE,{"disambiguationData":[TD([[subQ2,-1.0]])],"derivedFrom":subQ1}),1.0]])]});}
            var Q42;
            {var subQ0=sQuery(id+"F5.wireOp",EDGE,"E10.3.0.1");var subQ1=sQuery(id+"F5.wireOp",EDGE,"E6");var subQ2=makeQuery(id+"F5.imprint","INTERSECT",VERTEX,{"disambiguationData":[OD(0.0)],"derivedFrom":[subQ1,subQ0]});Q42=makeQuery(id+"F5.imprint","IMPRINT",FACE,{"disambiguationData":[TD([[makeQuery(id+"F5.imprint","IMPRINT",EDGE,{"disambiguationData":[TD([[subQ2,-1.0]])],"derivedFrom":subQ1}),1.0]])]});}
            var Q43;
            {var subQ0=sQuery(id+"F5.wireOp",EDGE,"E10.2.0.1");var subQ1=sQuery(id+"F5.wireOp",EDGE,"E6");var subQ2=makeQuery(id+"F5.imprint","INTERSECT",VERTEX,{"disambiguationData":[OD(0.0)],"derivedFrom":[subQ1,subQ0]});Q43=makeQuery(id+"F5.imprint","IMPRINT",FACE,{"disambiguationData":[TD([[makeQuery(id+"F5.imprint","IMPRINT",EDGE,{"disambiguationData":[TD([[subQ2,-1.0]])],"derivedFrom":subQ1}),-1.0]])]});}
            var Q44;
            {var subQ0=sQuery(id+"F5.wireOp",EDGE,"E10.2.0.1");var subQ1=sQuery(id+"F5.wireOp",EDGE,"E6");var subQ2=makeQuery(id+"F5.imprint","INTERSECT",VERTEX,{"disambiguationData":[OD(0.0)],"derivedFrom":[subQ1,subQ0]});Q44=makeQuery(id+"F5.imprint","IMPRINT",FACE,{"disambiguationData":[TD([[makeQuery(id+"F5.imprint","IMPRINT",EDGE,{"disambiguationData":[TD([[subQ2,-1.0]])],"derivedFrom":subQ1}),1.0]])]});}
            var Q45;
            {var subQ0=sQuery(id+"F5.wireOp",EDGE,"E10.1.0.1");var subQ1=sQuery(id+"F5.wireOp",EDGE,"E6");var subQ2=makeQuery(id+"F5.imprint","INTERSECT",VERTEX,{"disambiguationData":[OD(0.0)],"derivedFrom":[subQ1,subQ0]});Q45=makeQuery(id+"F5.imprint","IMPRINT",FACE,{"disambiguationData":[TD([[makeQuery(id+"F5.imprint","IMPRINT",EDGE,{"disambiguationData":[TD([[subQ2,-1.0]])],"derivedFrom":subQ1}),1.0]])]});}
            var Q46;
            {var subQ0=sQuery(id+"F5.wireOp",EDGE,"E10.3.0.1");var subQ1=sQuery(id+"F5.wireOp",EDGE,"E6");var subQ2=makeQuery(id+"F5.imprint","INTERSECT",VERTEX,{"disambiguationData":[OD(0.0)],"derivedFrom":[subQ1,subQ0]});Q46=makeQuery(id+"F5.imprint","IMPRINT",FACE,{"disambiguationData":[TD([[makeQuery(id+"F5.imprint","IMPRINT",EDGE,{"disambiguationData":[TD([[subQ2,-1.0]])],"derivedFrom":subQ1}),-1.0]])]});}
            var Q47;
            {var subQ0=sQuery(id+"F5.wireOp",EDGE,"E10.1.0.1");var subQ1=sQuery(id+"F5.wireOp",EDGE,"E6");var subQ2=makeQuery(id+"F5.imprint","INTERSECT",VERTEX,{"disambiguationData":[OD(0.0)],"derivedFrom":[subQ1,subQ0]});Q47=makeQuery(id+"F5.imprint","IMPRINT",FACE,{"disambiguationData":[TD([[makeQuery(id+"F5.imprint","IMPRINT",EDGE,{"disambiguationData":[TD([[subQ2,-1.0]])],"derivedFrom":subQ1}),-1.0]])]});}
            extrude(context, id + "F6", {"entities" : qUnion([Q0, Q1, Q2, Q3, Q4, Q5, Q6, Q7, Q8, Q9, Q10, Q11, Q12, Q13, Q14, Q15, Q16, Q17, Q18, Q19, Q20, Q21, Q22, Q23, Q24, Q25, Q26, Q27, Q28, Q29, Q30, Q31, Q32, Q33, Q34, Q35, Q36, Q37, Q38, Q39, Q40, Q41, Q42, Q43, Q44, Q45, Q46, Q47]), "operationType" : NewBodyOperationType.REMOVE, "oppositeDirection" : true, "depth" : 25 * mm, "offsetDistance" : 25 * mm});
        }
        {
            var Q0;
            Q0=makeQuery(id+"F1.opExtrude","CAP_FACE",FACE,{"disambiguationData":[OSD([sQuery(id+"F0.wireOp",EDGE,"E0.bottom"),sQuery(id+"F0.wireOp",EDGE,"E0.top"),sQuery(id+"F0.wireOp",EDGE,"E0.left"),sQuery(id+"F0.wireOp",EDGE,"E0.right")])],"isStart":true});
            var sketch = newSketch(context, id + "F7", { "sketchPlane" : qUnion([Q0])});
            skCircle(sketch, "E11", {"center": v(-123.8, 95) * mm, "radius": 2.5 * mm});
            skLineSegment(sketch, "E12", {"start": v(-147.5, 95) * mm, "end": v(147.5, 95) * mm});
            skCircle(sketch, "E13.1.0.0", {"center": v(-101.8, 95) * mm, "radius": 2.5 * mm});
            skCircle(sketch, "E13.2.0.0", {"center": v(-79.8, 95) * mm, "radius": 2.5 * mm});
            skCircle(sketch, "E13.3.0.0", {"center": v(-57.8, 95) * mm, "radius": 2.5 * mm});
            skCircle(sketch, "E13.4.0.0", {"center": v(-35.8, 95) * mm, "radius": 2.5 * mm});
            skCircle(sketch, "E13.5.0.0", {"center": v(-13.8, 95) * mm, "radius": 2.5 * mm});
            skCircle(sketch, "E13.6.0.0", {"center": v(8.2, 95) * mm, "radius": 2.5 * mm});
            skCircle(sketch, "E13.7.0.0", {"center": v(30.2, 95) * mm, "radius": 2.5 * mm});
            skCircle(sketch, "E13.8.0.0", {"center": v(52.2, 95) * mm, "radius": 2.5 * mm});
            skCircle(sketch, "E13.9.0.0", {"center": v(74.2, 95) * mm, "radius": 2.5 * mm});
            skCircle(sketch, "E13.10.0.0", {"center": v(96.2, 95) * mm, "radius": 2.5 * mm});
            skCircle(sketch, "E13.11.0.0", {"center": v(118.2, 95) * mm, "radius": 2.5 * mm});
            skLineSegment(sketch, "E13.direction1", {"start": v(-123.8, 95) * mm, "end": v(-101.8, 95) * mm, "construction": true});
            skSolve(sketch);
        }
        {
            var Q0;
            {var subQ0=sQuery(id+"F7.wireOp",EDGE,"E12");var subQ1=sQuery(id+"F7.wireOp",EDGE,"E11");var subQ2=makeQuery(id+"F7.imprint","INTERSECT",VERTEX,{"disambiguationData":[OD(0.0)],"derivedFrom":[subQ1,subQ0]});Q0=makeQuery(id+"F7.imprint","IMPRINT",FACE,{"disambiguationData":[TD([[makeQuery(id+"F7.imprint","IMPRINT",EDGE,{"disambiguationData":[TD([[subQ2,1.0]])],"derivedFrom":subQ1}),1.0]])]});}
            var Q1;
            {var subQ0=sQuery(id+"F7.wireOp",EDGE,"E12");var subQ1=sQuery(id+"F7.wireOp",EDGE,"E11");var subQ2=makeQuery(id+"F7.imprint","INTERSECT",VERTEX,{"disambiguationData":[OD(0.0)],"derivedFrom":[subQ1,subQ0]});Q1=makeQuery(id+"F7.imprint","IMPRINT",FACE,{"disambiguationData":[TD([[makeQuery(id+"F7.imprint","IMPRINT",EDGE,{"disambiguationData":[TD([[subQ2,-1.0]])],"derivedFrom":subQ1}),1.0]])]});}
            var Q2;
            {var subQ0=sQuery(id+"F7.wireOp",EDGE,"E13.1.0.0");var subQ1=sQuery(id+"F7.wireOp",EDGE,"E12");var subQ2=makeQuery(id+"F7.imprint","INTERSECT",VERTEX,{"disambiguationData":[OD(0.0)],"derivedFrom":[subQ1,subQ0]});Q2=makeQuery(id+"F7.imprint","IMPRINT",FACE,{"disambiguationData":[TD([[makeQuery(id+"F7.imprint","IMPRINT",EDGE,{"disambiguationData":[TD([[subQ2,-1.0]])],"derivedFrom":subQ1}),1.0]])]});}
            var Q3;
            {var subQ0=sQuery(id+"F7.wireOp",EDGE,"E13.1.0.0");var subQ1=sQuery(id+"F7.wireOp",EDGE,"E12");var subQ2=makeQuery(id+"F7.imprint","INTERSECT",VERTEX,{"disambiguationData":[OD(0.0)],"derivedFrom":[subQ1,subQ0]});Q3=makeQuery(id+"F7.imprint","IMPRINT",FACE,{"disambiguationData":[TD([[makeQuery(id+"F7.imprint","IMPRINT",EDGE,{"disambiguationData":[TD([[subQ2,-1.0]])],"derivedFrom":subQ1}),-1.0]])]});}
            var Q4;
            {var subQ0=sQuery(id+"F7.wireOp",EDGE,"E13.2.0.0");var subQ1=sQuery(id+"F7.wireOp",EDGE,"E12");var subQ2=makeQuery(id+"F7.imprint","INTERSECT",VERTEX,{"disambiguationData":[OD(0.0)],"derivedFrom":[subQ1,subQ0]});Q4=makeQuery(id+"F7.imprint","IMPRINT",FACE,{"disambiguationData":[TD([[makeQuery(id+"F7.imprint","IMPRINT",EDGE,{"disambiguationData":[TD([[subQ2,-1.0]])],"derivedFrom":subQ1}),-1.0]])]});}
            var Q5;
            {var subQ0=sQuery(id+"F7.wireOp",EDGE,"E13.2.0.0");var subQ1=sQuery(id+"F7.wireOp",EDGE,"E12");var subQ2=makeQuery(id+"F7.imprint","INTERSECT",VERTEX,{"disambiguationData":[OD(0.0)],"derivedFrom":[subQ1,subQ0]});Q5=makeQuery(id+"F7.imprint","IMPRINT",FACE,{"disambiguationData":[TD([[makeQuery(id+"F7.imprint","IMPRINT",EDGE,{"disambiguationData":[TD([[subQ2,-1.0]])],"derivedFrom":subQ1}),1.0]])]});}
            var Q6;
            {var subQ0=sQuery(id+"F7.wireOp",EDGE,"E13.3.0.0");var subQ1=sQuery(id+"F7.wireOp",EDGE,"E12");var subQ2=makeQuery(id+"F7.imprint","INTERSECT",VERTEX,{"disambiguationData":[OD(0.0)],"derivedFrom":[subQ1,subQ0]});Q6=makeQuery(id+"F7.imprint","IMPRINT",FACE,{"disambiguationData":[TD([[makeQuery(id+"F7.imprint","IMPRINT",EDGE,{"disambiguationData":[TD([[subQ2,-1.0]])],"derivedFrom":subQ1}),1.0]])]});}
            var Q7;
            {var subQ0=sQuery(id+"F7.wireOp",EDGE,"E13.3.0.0");var subQ1=sQuery(id+"F7.wireOp",EDGE,"E12");var subQ2=makeQuery(id+"F7.imprint","INTERSECT",VERTEX,{"disambiguationData":[OD(0.0)],"derivedFrom":[subQ1,subQ0]});Q7=makeQuery(id+"F7.imprint","IMPRINT",FACE,{"disambiguationData":[TD([[makeQuery(id+"F7.imprint","IMPRINT",EDGE,{"disambiguationData":[TD([[subQ2,-1.0]])],"derivedFrom":subQ1}),-1.0]])]});}
            var Q8;
            {var subQ0=sQuery(id+"F7.wireOp",EDGE,"E13.4.0.0");var subQ1=sQuery(id+"F7.wireOp",EDGE,"E12");var subQ2=makeQuery(id+"F7.imprint","INTERSECT",VERTEX,{"disambiguationData":[OD(0.0)],"derivedFrom":[subQ1,subQ0]});Q8=makeQuery(id+"F7.imprint","IMPRINT",FACE,{"disambiguationData":[TD([[makeQuery(id+"F7.imprint","IMPRINT",EDGE,{"disambiguationData":[TD([[subQ2,-1.0]])],"derivedFrom":subQ1}),1.0]])]});}
            var Q9;
            {var subQ0=sQuery(id+"F7.wireOp",EDGE,"E13.4.0.0");var subQ1=sQuery(id+"F7.wireOp",EDGE,"E12");var subQ2=makeQuery(id+"F7.imprint","INTERSECT",VERTEX,{"disambiguationData":[OD(0.0)],"derivedFrom":[subQ1,subQ0]});Q9=makeQuery(id+"F7.imprint","IMPRINT",FACE,{"disambiguationData":[TD([[makeQuery(id+"F7.imprint","IMPRINT",EDGE,{"disambiguationData":[TD([[subQ2,-1.0]])],"derivedFrom":subQ1}),-1.0]])]});}
            var Q10;
            {var subQ0=sQuery(id+"F7.wireOp",EDGE,"E13.5.0.0");var subQ1=sQuery(id+"F7.wireOp",EDGE,"E12");var subQ2=makeQuery(id+"F7.imprint","INTERSECT",VERTEX,{"disambiguationData":[OD(0.0)],"derivedFrom":[subQ1,subQ0]});Q10=makeQuery(id+"F7.imprint","IMPRINT",FACE,{"disambiguationData":[TD([[makeQuery(id+"F7.imprint","IMPRINT",EDGE,{"disambiguationData":[TD([[subQ2,-1.0]])],"derivedFrom":subQ1}),1.0]])]});}
            var Q11;
            {var subQ0=sQuery(id+"F7.wireOp",EDGE,"E13.5.0.0");var subQ1=sQuery(id+"F7.wireOp",EDGE,"E12");var subQ2=makeQuery(id+"F7.imprint","INTERSECT",VERTEX,{"disambiguationData":[OD(0.0)],"derivedFrom":[subQ1,subQ0]});Q11=makeQuery(id+"F7.imprint","IMPRINT",FACE,{"disambiguationData":[TD([[makeQuery(id+"F7.imprint","IMPRINT",EDGE,{"disambiguationData":[TD([[subQ2,-1.0]])],"derivedFrom":subQ1}),-1.0]])]});}
            var Q12;
            {var subQ0=sQuery(id+"F7.wireOp",EDGE,"E13.6.0.0");var subQ1=sQuery(id+"F7.wireOp",EDGE,"E12");var subQ2=makeQuery(id+"F7.imprint","INTERSECT",VERTEX,{"disambiguationData":[OD(0.0)],"derivedFrom":[subQ1,subQ0]});Q12=makeQuery(id+"F7.imprint","IMPRINT",FACE,{"disambiguationData":[TD([[makeQuery(id+"F7.imprint","IMPRINT",EDGE,{"disambiguationData":[TD([[subQ2,-1.0]])],"derivedFrom":subQ1}),1.0]])]});}
            var Q13;
            {var subQ0=sQuery(id+"F7.wireOp",EDGE,"E13.6.0.0");var subQ1=sQuery(id+"F7.wireOp",EDGE,"E12");var subQ2=makeQuery(id+"F7.imprint","INTERSECT",VERTEX,{"disambiguationData":[OD(0.0)],"derivedFrom":[subQ1,subQ0]});Q13=makeQuery(id+"F7.imprint","IMPRINT",FACE,{"disambiguationData":[TD([[makeQuery(id+"F7.imprint","IMPRINT",EDGE,{"disambiguationData":[TD([[subQ2,-1.0]])],"derivedFrom":subQ1}),-1.0]])]});}
            var Q14;
            {var subQ0=sQuery(id+"F7.wireOp",EDGE,"E13.7.0.0");var subQ1=sQuery(id+"F7.wireOp",EDGE,"E12");var subQ2=makeQuery(id+"F7.imprint","INTERSECT",VERTEX,{"disambiguationData":[OD(0.0)],"derivedFrom":[subQ1,subQ0]});Q14=makeQuery(id+"F7.imprint","IMPRINT",FACE,{"disambiguationData":[TD([[makeQuery(id+"F7.imprint","IMPRINT",EDGE,{"disambiguationData":[TD([[subQ2,-1.0]])],"derivedFrom":subQ1}),1.0]])]});}
            var Q15;
            {var subQ0=sQuery(id+"F7.wireOp",EDGE,"E13.7.0.0");var subQ1=sQuery(id+"F7.wireOp",EDGE,"E12");var subQ2=makeQuery(id+"F7.imprint","INTERSECT",VERTEX,{"disambiguationData":[OD(0.0)],"derivedFrom":[subQ1,subQ0]});Q15=makeQuery(id+"F7.imprint","IMPRINT",FACE,{"disambiguationData":[TD([[makeQuery(id+"F7.imprint","IMPRINT",EDGE,{"disambiguationData":[TD([[subQ2,-1.0]])],"derivedFrom":subQ1}),-1.0]])]});}
            var Q16;
            {var subQ0=sQuery(id+"F7.wireOp",EDGE,"E13.8.0.0");var subQ1=sQuery(id+"F7.wireOp",EDGE,"E12");var subQ2=makeQuery(id+"F7.imprint","INTERSECT",VERTEX,{"disambiguationData":[OD(0.0)],"derivedFrom":[subQ1,subQ0]});Q16=makeQuery(id+"F7.imprint","IMPRINT",FACE,{"disambiguationData":[TD([[makeQuery(id+"F7.imprint","IMPRINT",EDGE,{"disambiguationData":[TD([[subQ2,-1.0]])],"derivedFrom":subQ1}),1.0]])]});}
            var Q17;
            {var subQ0=sQuery(id+"F7.wireOp",EDGE,"E13.8.0.0");var subQ1=sQuery(id+"F7.wireOp",EDGE,"E12");var subQ2=makeQuery(id+"F7.imprint","INTERSECT",VERTEX,{"disambiguationData":[OD(0.0)],"derivedFrom":[subQ1,subQ0]});Q17=makeQuery(id+"F7.imprint","IMPRINT",FACE,{"disambiguationData":[TD([[makeQuery(id+"F7.imprint","IMPRINT",EDGE,{"disambiguationData":[TD([[subQ2,-1.0]])],"derivedFrom":subQ1}),-1.0]])]});}
            var Q18;
            {var subQ0=sQuery(id+"F7.wireOp",EDGE,"E13.9.0.0");var subQ1=sQuery(id+"F7.wireOp",EDGE,"E12");var subQ2=makeQuery(id+"F7.imprint","INTERSECT",VERTEX,{"disambiguationData":[OD(0.0)],"derivedFrom":[subQ1,subQ0]});Q18=makeQuery(id+"F7.imprint","IMPRINT",FACE,{"disambiguationData":[TD([[makeQuery(id+"F7.imprint","IMPRINT",EDGE,{"disambiguationData":[TD([[subQ2,-1.0]])],"derivedFrom":subQ1}),1.0]])]});}
            var Q19;
            {var subQ0=sQuery(id+"F7.wireOp",EDGE,"E13.9.0.0");var subQ1=sQuery(id+"F7.wireOp",EDGE,"E12");var subQ2=makeQuery(id+"F7.imprint","INTERSECT",VERTEX,{"disambiguationData":[OD(0.0)],"derivedFrom":[subQ1,subQ0]});Q19=makeQuery(id+"F7.imprint","IMPRINT",FACE,{"disambiguationData":[TD([[makeQuery(id+"F7.imprint","IMPRINT",EDGE,{"disambiguationData":[TD([[subQ2,-1.0]])],"derivedFrom":subQ1}),-1.0]])]});}
            var Q20;
            {var subQ0=sQuery(id+"F7.wireOp",EDGE,"E13.10.0.0");var subQ1=sQuery(id+"F7.wireOp",EDGE,"E12");var subQ2=makeQuery(id+"F7.imprint","INTERSECT",VERTEX,{"disambiguationData":[OD(0.0)],"derivedFrom":[subQ1,subQ0]});Q20=makeQuery(id+"F7.imprint","IMPRINT",FACE,{"disambiguationData":[TD([[makeQuery(id+"F7.imprint","IMPRINT",EDGE,{"disambiguationData":[TD([[subQ2,-1.0]])],"derivedFrom":subQ1}),1.0]])]});}
            var Q21;
            {var subQ0=sQuery(id+"F7.wireOp",EDGE,"E13.10.0.0");var subQ1=sQuery(id+"F7.wireOp",EDGE,"E12");var subQ2=makeQuery(id+"F7.imprint","INTERSECT",VERTEX,{"disambiguationData":[OD(0.0)],"derivedFrom":[subQ1,subQ0]});Q21=makeQuery(id+"F7.imprint","IMPRINT",FACE,{"disambiguationData":[TD([[makeQuery(id+"F7.imprint","IMPRINT",EDGE,{"disambiguationData":[TD([[subQ2,-1.0]])],"derivedFrom":subQ1}),-1.0]])]});}
            var Q22;
            {var subQ0=sQuery(id+"F7.wireOp",EDGE,"E13.11.0.0");var subQ1=sQuery(id+"F7.wireOp",EDGE,"E12");var subQ2=makeQuery(id+"F7.imprint","INTERSECT",VERTEX,{"disambiguationData":[OD(0.0)],"derivedFrom":[subQ1,subQ0]});Q22=makeQuery(id+"F7.imprint","IMPRINT",FACE,{"disambiguationData":[TD([[makeQuery(id+"F7.imprint","IMPRINT",EDGE,{"disambiguationData":[TD([[subQ2,-1.0]])],"derivedFrom":subQ1}),1.0]])]});}
            var Q23;
            {var subQ0=sQuery(id+"F7.wireOp",EDGE,"E13.11.0.0");var subQ1=sQuery(id+"F7.wireOp",EDGE,"E12");var subQ2=makeQuery(id+"F7.imprint","INTERSECT",VERTEX,{"disambiguationData":[OD(0.0)],"derivedFrom":[subQ1,subQ0]});Q23=makeQuery(id+"F7.imprint","IMPRINT",FACE,{"disambiguationData":[TD([[makeQuery(id+"F7.imprint","IMPRINT",EDGE,{"disambiguationData":[TD([[subQ2,-1.0]])],"derivedFrom":subQ1}),-1.0]])]});}
            extrude(context, id + "F8", {"entities" : qUnion([Q0, Q1, Q2, Q3, Q4, Q5, Q6, Q7, Q8, Q9, Q10, Q11, Q12, Q13, Q14, Q15, Q16, Q17, Q18, Q19, Q20, Q21, Q22, Q23]), "operationType" : NewBodyOperationType.REMOVE, "oppositeDirection" : true, "depth" : 25 * mm, "offsetDistance" : 25 * mm});
        }
        {
            var Q0;
            Q0=makeQuery(id+"F1.opExtrude","CAP_FACE",FACE,{"disambiguationData":[OSD([sQuery(id+"F0.wireOp",EDGE,"E0.bottom"),sQuery(id+"F0.wireOp",EDGE,"E0.top"),sQuery(id+"F0.wireOp",EDGE,"E0.left"),sQuery(id+"F0.wireOp",EDGE,"E0.right")])],"isStart":true});
            var sketch = newSketch(context, id + "F9", { "sketchPlane" : qUnion([Q0])});
            skCircle(sketch, "E14", {"center": v(-12.5, 0) * mm, "radius": 7 * mm});
            skCircle(sketch, "E15", {"center": v(-12.5, -30) * mm, "radius": 7.5 * mm});
            skCircle(sketch, "E16", {"center": v(-12.5, -15) * mm, "radius": 2.5 * mm});
            skCircle(sketch, "E17.1.0.0", {"center": v(-37.5, 0) * mm, "radius": 7 * mm});
            skCircle(sketch, "E17.1.0.1", {"center": v(-37.5, -15) * mm, "radius": 2.5 * mm});
            skCircle(sketch, "E17.1.0.2", {"center": v(-37.5, -30) * mm, "radius": 7.5 * mm});
            skLineSegment(sketch, "E17.direction1", {"start": v(-12.5, 0) * mm, "end": v(-37.5, 0) * mm, "construction": true});
            skCircle(sketch, "E18.1.0.0", {"center": v(12.5, 0) * mm, "radius": 7 * mm});
            skCircle(sketch, "E18.1.0.1", {"center": v(12.5, -15) * mm, "radius": 2.5 * mm});
            skCircle(sketch, "E18.1.0.2", {"center": v(12.5, -30) * mm, "radius": 7.5 * mm});
            skCircle(sketch, "E18.2.0.0", {"center": v(37.5, 0) * mm, "radius": 7 * mm});
            skCircle(sketch, "E18.2.0.1", {"center": v(37.5, -15) * mm, "radius": 2.5 * mm});
            skCircle(sketch, "E18.2.0.2", {"center": v(37.5, -30) * mm, "radius": 7.5 * mm});
            skLineSegment(sketch, "E18.direction1", {"start": v(-12.5, 0) * mm, "end": v(12.5, 0) * mm, "construction": true});
            skSolve(sketch);
        }
        {
            var Q0;
            Q0=makeQuery(id+"F9.imprint","IMPRINT",FACE,{"disambiguationData":[TD([[makeQuery(id+"F9.imprint","IMPRINT",EDGE,{"derivedFrom":sQuery(id+"F9.wireOp",EDGE,"E17.2.0.0")}),1.0]])]});
            var Q1;
            Q1=makeQuery(id+"F9.imprint","IMPRINT",FACE,{"disambiguationData":[TD([[makeQuery(id+"F9.imprint","IMPRINT",EDGE,{"derivedFrom":sQuery(id+"F9.wireOp",EDGE,"E17.1.0.2")}),1.0]])]});
            var Q2;
            Q2=makeQuery(id+"F9.imprint","IMPRINT",FACE,{"disambiguationData":[TD([[makeQuery(id+"F9.imprint","IMPRINT",EDGE,{"derivedFrom":sQuery(id+"F9.wireOp",EDGE,"E17.2.0.2")}),1.0]])]});
            var Q3;
            Q3=makeQuery(id+"F9.imprint","IMPRINT",FACE,{"disambiguationData":[TD([[makeQuery(id+"F9.imprint","IMPRINT",EDGE,{"derivedFrom":sQuery(id+"F9.wireOp",EDGE,"E17.3.0.2")}),1.0]])]});
            var Q4;
            Q4=makeQuery(id+"F9.imprint","IMPRINT",FACE,{"disambiguationData":[TD([[makeQuery(id+"F9.imprint","IMPRINT",EDGE,{"derivedFrom":sQuery(id+"F9.wireOp",EDGE,"E17.1.0.0")}),1.0]])]});
            var Q5;
            Q5=makeQuery(id+"F9.imprint","IMPRINT",FACE,{"disambiguationData":[TD([[makeQuery(id+"F9.imprint","IMPRINT",EDGE,{"derivedFrom":sQuery(id+"F9.wireOp",EDGE,"E18.3.0.2")}),1.0]])]});
            var Q6;
            Q6=makeQuery(id+"F9.imprint","IMPRINT",FACE,{"disambiguationData":[TD([[makeQuery(id+"F9.imprint","IMPRINT",EDGE,{"derivedFrom":sQuery(id+"F9.wireOp",EDGE,"E18.1.0.0")}),1.0]])]});
            var Q7;
            Q7=makeQuery(id+"F9.imprint","IMPRINT",FACE,{"disambiguationData":[TD([[makeQuery(id+"F9.imprint","IMPRINT",EDGE,{"derivedFrom":sQuery(id+"F9.wireOp",EDGE,"E17.3.0.0")}),1.0]])]});
            var Q8;
            Q8=makeQuery(id+"F9.imprint","IMPRINT",FACE,{"disambiguationData":[TD([[makeQuery(id+"F9.imprint","IMPRINT",EDGE,{"derivedFrom":sQuery(id+"F9.wireOp",EDGE,"E18.3.0.0")}),1.0]])]});
            var Q9;
            Q9=makeQuery(id+"F9.imprint","IMPRINT",FACE,{"disambiguationData":[TD([[makeQuery(id+"F9.imprint","IMPRINT",EDGE,{"derivedFrom":sQuery(id+"F9.wireOp",EDGE,"E18.2.0.2")}),1.0]])]});
            var Q10;
            Q10=makeQuery(id+"F9.imprint","IMPRINT",FACE,{"disambiguationData":[TD([[makeQuery(id+"F9.imprint","IMPRINT",EDGE,{"derivedFrom":sQuery(id+"F9.wireOp",EDGE,"E18.2.0.0")}),1.0]])]});
            var Q11;
            Q11=makeQuery(id+"F9.imprint","IMPRINT",FACE,{"disambiguationData":[TD([[makeQuery(id+"F9.imprint","IMPRINT",EDGE,{"derivedFrom":sQuery(id+"F9.wireOp",EDGE,"E18.1.0.2")}),1.0]])]});
            var Q12;
            Q12=makeQuery(id+"F9.imprint","IMPRINT",FACE,{"disambiguationData":[TD([[makeQuery(id+"F9.imprint","IMPRINT",EDGE,{"derivedFrom":sQuery(id+"F9.wireOp",EDGE,"E15")}),1.0]])]});
            var Q13;
            Q13=makeQuery(id+"F9.imprint","IMPRINT",FACE,{"disambiguationData":[TD([[makeQuery(id+"F9.imprint","IMPRINT",EDGE,{"derivedFrom":sQuery(id+"F9.wireOp",EDGE,"E18.1.0.1")}),1.0]])]});
            var Q14;
            Q14=makeQuery(id+"F9.imprint","IMPRINT",FACE,{"disambiguationData":[TD([[makeQuery(id+"F9.imprint","IMPRINT",EDGE,{"derivedFrom":sQuery(id+"F9.wireOp",EDGE,"E16")}),1.0]])]});
            var Q15;
            Q15=makeQuery(id+"F9.imprint","IMPRINT",FACE,{"disambiguationData":[TD([[makeQuery(id+"F9.imprint","IMPRINT",EDGE,{"derivedFrom":sQuery(id+"F9.wireOp",EDGE,"E17.2.0.1")}),1.0]])]});
            var Q16;
            Q16=makeQuery(id+"F9.imprint","IMPRINT",FACE,{"disambiguationData":[TD([[makeQuery(id+"F9.imprint","IMPRINT",EDGE,{"derivedFrom":sQuery(id+"F9.wireOp",EDGE,"E17.1.0.1")}),1.0]])]});
            var Q17;
            Q17=makeQuery(id+"F9.imprint","IMPRINT",FACE,{"disambiguationData":[TD([[makeQuery(id+"F9.imprint","IMPRINT",EDGE,{"derivedFrom":sQuery(id+"F9.wireOp",EDGE,"E17.3.0.1")}),1.0]])]});
            var Q18;
            Q18=makeQuery(id+"F9.imprint","IMPRINT",FACE,{"disambiguationData":[TD([[makeQuery(id+"F9.imprint","IMPRINT",EDGE,{"derivedFrom":sQuery(id+"F9.wireOp",EDGE,"E18.3.0.1")}),1.0]])]});
            var Q19;
            Q19=makeQuery(id+"F9.imprint","IMPRINT",FACE,{"disambiguationData":[TD([[makeQuery(id+"F9.imprint","IMPRINT",EDGE,{"derivedFrom":sQuery(id+"F9.wireOp",EDGE,"E18.2.0.1")}),1.0]])]});
            var Q20;
            Q20=makeQuery(id+"F9.imprint","IMPRINT",FACE,{"disambiguationData":[TD([[makeQuery(id+"F9.imprint","IMPRINT",EDGE,{"derivedFrom":sQuery(id+"F9.wireOp",EDGE,"E14")}),1.0]])]});
            extrude(context, id + "F10", {"entities" : qUnion([Q0, Q1, Q2, Q3, Q4, Q5, Q6, Q7, Q8, Q9, Q10, Q11, Q12, Q13, Q14, Q15, Q16, Q17, Q18, Q19, Q20]), "operationType" : NewBodyOperationType.REMOVE, "oppositeDirection" : true, "depth" : 25 * mm, "offsetDistance" : 25 * mm});
        }
        {
            var Q0;
            Q0=makeQuery(id+"F1.opExtrude","CAP_FACE",FACE,{"disambiguationData":[OSD([sQuery(id+"F0.wireOp",EDGE,"E0.bottom"),sQuery(id+"F0.wireOp",EDGE,"E0.top"),sQuery(id+"F0.wireOp",EDGE,"E0.left"),sQuery(id+"F0.wireOp",EDGE,"E0.right")])],"isStart":true});
            var sketch = newSketch(context, id + "F11", { "sketchPlane" : qUnion([Q0])});
            skCircle(sketch, "E19", {"center": v(11, -75.93) * mm, "radius": 4 * mm});
            skCircle(sketch, "E20.0.1.0", {"center": v(11, -97.93) * mm, "radius": 4 * mm});
            skCircle(sketch, "E20.1.0.0", {"center": v(36, -75.93) * mm, "radius": 4 * mm});
            skCircle(sketch, "E20.1.1.0", {"center": v(36, -97.93) * mm, "radius": 4 * mm});
            skLineSegment(sketch, "E20.direction1", {"start": v(11, -75.93) * mm, "end": v(36, -75.93) * mm, "construction": true});
            skLineSegment(sketch, "E20.direction2", {"start": v(11, -75.93) * mm, "end": v(11, -97.93) * mm, "construction": true});
            skCircle(sketch, "E21.0.2.0", {"center": v(61, -75.93) * mm, "radius": 4 * mm});
            skCircle(sketch, "E21.0.2.1", {"center": v(61, -97.93) * mm, "radius": 4 * mm});
            skCircle(sketch, "E22.1.0.0", {"center": v(-11, -75.83) * mm, "radius": 4 * mm});
            skCircle(sketch, "E22.1.0.1", {"center": v(-11, -97.83) * mm, "radius": 4 * mm});
            skCircle(sketch, "E22.2.0.0", {"center": v(-33, -75.73) * mm, "radius": 4 * mm});
            skCircle(sketch, "E22.2.0.1", {"center": v(-33, -97.73) * mm, "radius": 4 * mm});
            skCircle(sketch, "E22.3.0.0", {"center": v(-55, -75.62) * mm, "radius": 4 * mm});
            skCircle(sketch, "E22.3.0.1", {"center": v(-55, -97.62) * mm, "radius": 4 * mm});
            skLineSegment(sketch, "E22.direction1", {"start": v(11, -97.93) * mm, "end": v(-11, -97.83) * mm, "construction": true});
            skSolve(sketch);
        }
        {
            var Q0;
            Q0=makeQuery(id+"F11.imprint","IMPRINT",FACE,{"disambiguationData":[TD([[makeQuery(id+"F11.imprint","IMPRINT",EDGE,{"derivedFrom":sQuery(id+"F11.wireOp",EDGE,"E19")}),-1.0]])]});
            extrude(context, id + "F12", {"entities" : qUnion([Q0]), "operationType" : NewBodyOperationType.INTERSECT, "surfaceOperationType" : NewSurfaceOperationType.ADD, "oppositeDirection" : true, "depth" : 2 * mm, "offsetDistance" : 25 * mm});
        }
    });
